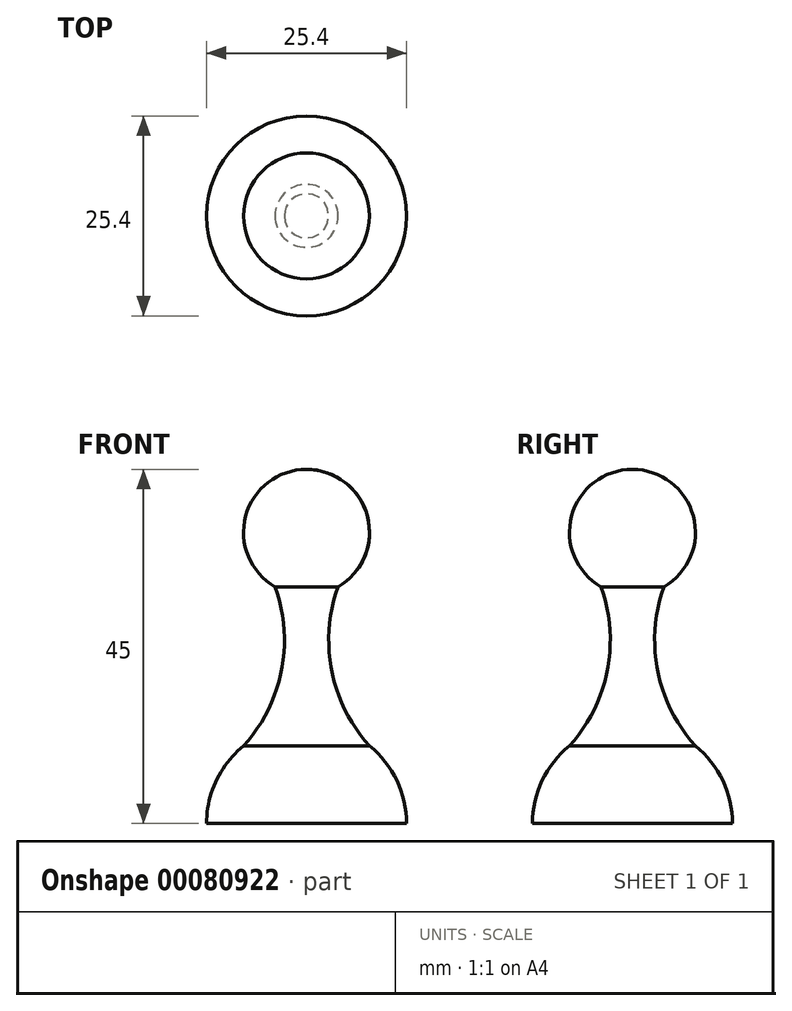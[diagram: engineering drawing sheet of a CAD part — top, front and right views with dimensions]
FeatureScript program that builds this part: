
annotation { "Feature Type Name" : "Feature", "Feature Type Description" : "" }
export const myFeature = defineFeature(function(context is Context, id is Id, definition is map)
    precondition{}
    {
        {
            var Q0;
            Q0=qCreatedBy(makeId("Front.planeOp"),FACE);
            var sketch = newSketch(context, id + "F0", { "sketchPlane" : qUnion([Q0])});
            skLineSegment(sketch, "E0", {"start": v(0, 0) * mm, "end": v(0, 45) * mm});
            skLineSegment(sketch, "E1", {"start": v(0, 0) * mm, "end": v(12.7, 0) * mm});
            skArc(sketch, "E2", {"start": v(12.7, 0) * mm, "mid": v(11.46, 5.46) * mm, "end": v(8, 9.86) * mm});
            skArc(sketch, "E3", {"start": v(0, 45) * mm, "mid": v(7.73, 39.07) * mm, "end": v(4, 30.07) * mm});
            skArc(sketch, "E4", {"start": v(4, 30.07) * mm, "mid": v(3.2, 19.41) * mm, "end": v(8, 9.86) * mm});
            skSolve(sketch);
        }
        {
            var Q0;
            Q0 = qSketchRegion(id + "F0", true);
            var Q1;
            Q1=sQuery(id+"F0.wireOp",EDGE,"E0");
            revolve(context, id + "F1", {"entities" : qUnion([Q0]), "axis" : qUnion([Q1]), "revolveType" : RevolveType.FULL});
        }
    });
